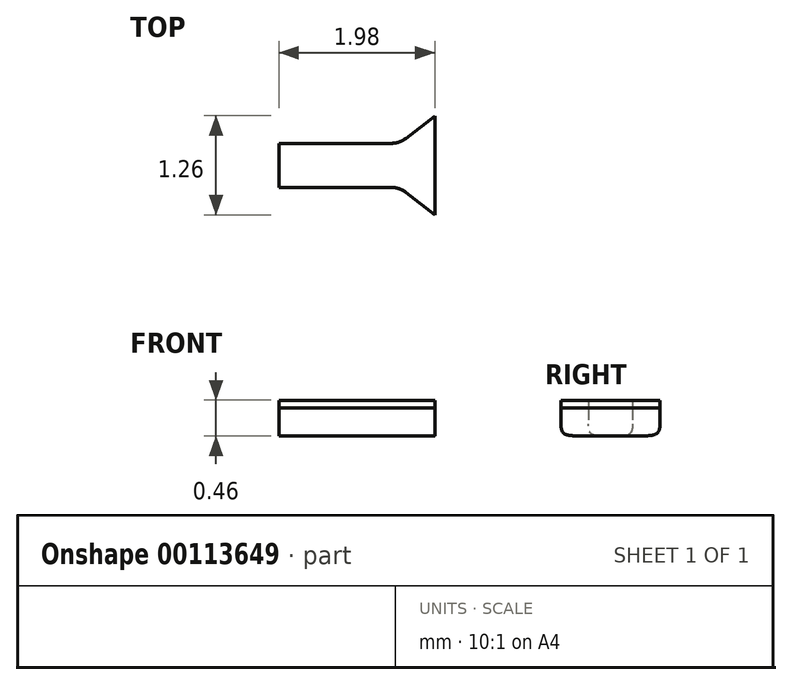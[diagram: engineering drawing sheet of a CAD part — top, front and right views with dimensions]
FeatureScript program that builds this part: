
annotation { "Feature Type Name" : "Feature", "Feature Type Description" : "" }
export const myFeature = defineFeature(function(context is Context, id is Id, definition is map)
    precondition{}
    {
        {
            var Q0;
            Q0=qCreatedBy(makeId("Top.planeOp"),FACE);
            var sketch = newSketch(context, id + "F0", { "sketchPlane" : qUnion([Q0])});
            skLineSegment(sketch, "E0", {"start": v(-7, 0) * mm, "end": v(-7, 1.25) * mm});
            skLineSegment(sketch, "E1", {"start": v(-7, 1.25) * mm, "end": v(-2.5, 1.25) * mm});
            skLineSegment(sketch, "E2", {"start": v(-2.5, 1.25) * mm, "end": v(-1.33, 0.34) * mm});
            skLineSegment(sketch, "E3", {"start": v(-1.15, 0.28) * mm, "end": v(0, 0.28) * mm});
            skPoint(sketch, "E4.visualSharp", {"position": v(-1.25, 0.28) * mm});
            skArc(sketch, "E4.filletArc", {"start": v(-1.33, 0.34) * mm, "mid": v(-1.24, 0.3) * mm, "end": v(-1.15, 0.28) * mm});
            skLineSegment(sketch, "E5.MirrorCS", {"start": v(-7, 0) * mm, "end": v(-7, -1.25) * mm});
            skLineSegment(sketch, "E6.MirrorCS", {"start": v(-7, -1.25) * mm, "end": v(-2.5, -1.25) * mm});
            skLineSegment(sketch, "E7.MirrorCS", {"start": v(-2.5, -1.25) * mm, "end": v(-1.33, -0.34) * mm});
            skLineSegment(sketch, "E8.MirrorCS", {"start": v(-1.15, -0.28) * mm, "end": v(0, -0.28) * mm});
            skArc(sketch, "E9.MirrorCS", {"start": v(-1.33, -0.34) * mm, "mid": v(-1.24, -0.3) * mm, "end": v(-1.15, -0.28) * mm});
            skCircle(sketch, "E10", {"center": v(-5, 0) * mm, "radius": 0.5 * mm});
            skArc(sketch, "E11.MirrorCS", {"start": v(1.33, -0.34) * mm, "mid": v(1.24, -0.3) * mm, "end": v(1.15, -0.28) * mm});
            skArc(sketch, "E12.MirrorCS", {"start": v(1.33, 0.34) * mm, "mid": v(1.24, 0.3) * mm, "end": v(1.15, 0.28) * mm});
            skLineSegment(sketch, "E13.MirrorCS", {"start": v(7, 0) * mm, "end": v(7, 1.25) * mm});
            skLineSegment(sketch, "E14.MirrorCS", {"start": v(7, 1.25) * mm, "end": v(2.5, 1.25) * mm});
            skLineSegment(sketch, "E15.MirrorCS", {"start": v(2.5, 1.25) * mm, "end": v(1.33, 0.34) * mm});
            skPoint(sketch, "E16.MirrorP", {"position": v(1.25, 0.28) * mm});
            skCircle(sketch, "E17.MirrorC", {"center": v(5, 0) * mm, "radius": 0.5 * mm});
            skLineSegment(sketch, "E18.MirrorCS", {"start": v(1.15, -0.28) * mm, "end": v(0, -0.28) * mm});
            skLineSegment(sketch, "E19.MirrorCS", {"start": v(2.5, -1.25) * mm, "end": v(1.33, -0.34) * mm});
            skLineSegment(sketch, "E20.MirrorCS", {"start": v(1.15, 0.28) * mm, "end": v(0, 0.28) * mm});
            skLineSegment(sketch, "E21.MirrorCS", {"start": v(7, 0) * mm, "end": v(7, -1.25) * mm});
            skLineSegment(sketch, "E22.MirrorCS", {"start": v(7, -1.25) * mm, "end": v(2.5, -1.25) * mm});
            skSolve(sketch);
        }
        {
            var Q0;
            Q0=makeQuery(id+"F0.imprint","IMPRINT",FACE,{"disambiguationData":[TD([[makeQuery(id+"F0.imprint","IMPRINT",EDGE,{"derivedFrom":sQuery(id+"F0.wireOp",EDGE,"E0")}),-1.0]])]});
            extrude(context, id + "F1", {"entities" : qUnion([Q0]), "depth" : 0.35 * mm, "offsetDistance" : 25 * mm, "symmetric" : true});
        }
        {
            var Q0;
            Q0=makeQuery(id+"F1.opExtrude","SWEPT_EDGE",EDGE,{"disambiguationData":[OSD([sQuery(id+"F0.wireOp",EDGE,"E6.MirrorCS"),sQuery(id+"F0.wireOp",EDGE,"E7.MirrorCS")])]});
            var Q1;
            Q1=makeQuery(id+"F1.opExtrude","SWEPT_EDGE",EDGE,{"disambiguationData":[OSD([sQuery(id+"F0.wireOp",EDGE,"E19.MirrorCS"),sQuery(id+"F0.wireOp",EDGE,"E22.MirrorCS")])]});
            var Q2;
            Q2=makeQuery(id+"F1.opExtrude","SWEPT_EDGE",EDGE,{"disambiguationData":[OSD([sQuery(id+"F0.wireOp",EDGE,"E1"),sQuery(id+"F0.wireOp",EDGE,"E2")])]});
            var Q3;
            Q3=makeQuery(id+"F1.opExtrude","SWEPT_EDGE",EDGE,{"disambiguationData":[OSD([sQuery(id+"F0.wireOp",EDGE,"E14.MirrorCS"),sQuery(id+"F0.wireOp",EDGE,"E15.MirrorCS")])]});
            fillet(context, id + "F2", {"entities" : qUnion([Q0, Q1, Q2, Q3]), "radius" : 0.3 * mm, "tangentPropagation" : true, "allowEdgeOverflow" : false});
        }
        {
            var Q0;
            Q0=qCreatedBy(makeId("Top.planeOp"),FACE);
            var sketch = newSketch(context, id + "F3", { "sketchPlane" : qUnion([Q0])});
            skLineSegment(sketch, "E23.bottom", {"start": v(-0.28, -1.5) * mm, "end": v(1.7, -1.5) * mm});
            skLineSegment(sketch, "E23.top", {"start": v(-0.28, 1.5) * mm, "end": v(1.7, 1.5) * mm});
            skLineSegment(sketch, "E23.left", {"start": v(-0.28, -1.5) * mm, "end": v(-0.28, 1.5) * mm});
            skLineSegment(sketch, "E23.right", {"start": v(1.7, -1.5) * mm, "end": v(1.7, 1.5) * mm});
            skSolve(sketch);
        }
        {
            var Q0;
            Q0=makeQuery(id+"F3.imprint","IMPRINT",FACE,{"disambiguationData":[TD([[makeQuery(id+"F3.imprint","IMPRINT",EDGE,{"derivedFrom":sQuery(id+"F3.wireOp",EDGE,"E23.bottom")}),1.0]])]});
            extrude(context, id + "F4", {"entities" : qUnion([Q0]), "depth" : 1 * mm, "offsetDistance" : 25 * mm, "symmetric" : true});
        }
        {
            var Q0;
            Q0=makeQuery(id+"F4.opExtrude","SWEPT_BODY",BODY,{"disambiguationData":[OSD([sQuery(id+"F3.wireOp",EDGE,"E23.bottom"),sQuery(id+"F3.wireOp",EDGE,"E23.top"),sQuery(id+"F3.wireOp",EDGE,"E23.right"),sQuery(id+"F3.wireOp",EDGE,"E23.left")])]});
            var Q1;
            Q1=makeQuery(id+"F1.opExtrude","SWEPT_BODY",BODY,{"disambiguationData":[OSD([sQuery(id+"F0.wireOp",EDGE,"E0"),sQuery(id+"F0.wireOp",EDGE,"E1"),sQuery(id+"F0.wireOp",EDGE,"E2"),sQuery(id+"F0.wireOp",EDGE,"E3"),sQuery(id+"F0.wireOp",EDGE,"E4.filletArc"),sQuery(id+"F0.wireOp",EDGE,"E5.MirrorCS"),sQuery(id+"F0.wireOp",EDGE,"E6.MirrorCS"),sQuery(id+"F0.wireOp",EDGE,"E7.MirrorCS"),sQuery(id+"F0.wireOp",EDGE,"E8.MirrorCS"),sQuery(id+"F0.wireOp",EDGE,"E9.MirrorCS"),sQuery(id+"F0.wireOp",EDGE,"E10"),sQuery(id+"F0.wireOp",EDGE,"E11.MirrorCS"),sQuery(id+"F0.wireOp",EDGE,"E12.MirrorCS"),sQuery(id+"F0.wireOp",EDGE,"E13.MirrorCS"),sQuery(id+"F0.wireOp",EDGE,"E14.MirrorCS"),sQuery(id+"F0.wireOp",EDGE,"E15.MirrorCS"),sQuery(id+"F0.wireOp",EDGE,"E17.MirrorC"),sQuery(id+"F0.wireOp",EDGE,"E18.MirrorCS"),sQuery(id+"F0.wireOp",EDGE,"E19.MirrorCS"),sQuery(id+"F0.wireOp",EDGE,"E20.MirrorCS"),sQuery(id+"F0.wireOp",EDGE,"E21.MirrorCS"),sQuery(id+"F0.wireOp",EDGE,"E22.MirrorCS")])]});
            booleanBodies(context, id + "F5", {"operationType" : BooleanOperationType.INTERSECTION, "tools" : qUnion([Q0, Q1])});
        }
        {
            var Q0;
            Q0=makeQuery(id+"F1.opExtrude","CAP_FACE",FACE,{"disambiguationData":[OSD([sQuery(id+"F0.wireOp",EDGE,"E0"),sQuery(id+"F0.wireOp",EDGE,"E1"),sQuery(id+"F0.wireOp",EDGE,"E2"),sQuery(id+"F0.wireOp",EDGE,"E3"),sQuery(id+"F0.wireOp",EDGE,"E4.filletArc"),sQuery(id+"F0.wireOp",EDGE,"E5.MirrorCS"),sQuery(id+"F0.wireOp",EDGE,"E6.MirrorCS"),sQuery(id+"F0.wireOp",EDGE,"E7.MirrorCS"),sQuery(id+"F0.wireOp",EDGE,"E8.MirrorCS"),sQuery(id+"F0.wireOp",EDGE,"E9.MirrorCS"),sQuery(id+"F0.wireOp",EDGE,"E10"),sQuery(id+"F0.wireOp",EDGE,"E11.MirrorCS"),sQuery(id+"F0.wireOp",EDGE,"E12.MirrorCS"),sQuery(id+"F0.wireOp",EDGE,"E13.MirrorCS"),sQuery(id+"F0.wireOp",EDGE,"E14.MirrorCS"),sQuery(id+"F0.wireOp",EDGE,"E15.MirrorCS"),sQuery(id+"F0.wireOp",EDGE,"E17.MirrorC"),sQuery(id+"F0.wireOp",EDGE,"E18.MirrorCS"),sQuery(id+"F0.wireOp",EDGE,"E19.MirrorCS"),sQuery(id+"F0.wireOp",EDGE,"E20.MirrorCS"),sQuery(id+"F0.wireOp",EDGE,"E21.MirrorCS"),sQuery(id+"F0.wireOp",EDGE,"E22.MirrorCS")])],"isStart":false});
            extrude(context, id + "F6", {"entities" : qUnion([Q0]), "depth" : 0.1 * mm, "offsetDistance" : 25 * mm});
        }
        {
            var Q0;
            Q0=makeQuery(id+"F5.opBoolean","COPY",EDGE,{"derivedFrom":makeQuery(id+"F1.opExtrude","CAP_EDGE",EDGE,{"disambiguationData":[OSD([sQuery(id+"F0.wireOp",EDGE,"E8.MirrorCS"),sQuery(id+"F0.wireOp",EDGE,"E18.MirrorCS")])],"isStart":false})});
            var Q1;
            Q1=makeQuery(id+"F5.opBoolean","COPY",EDGE,{"derivedFrom":makeQuery(id+"F1.opExtrude","CAP_EDGE",EDGE,{"disambiguationData":[OSD([sQuery(id+"F0.wireOp",EDGE,"E3"),sQuery(id+"F0.wireOp",EDGE,"E20.MirrorCS")])],"isStart":false})});
            var Q2;
            Q2=makeQuery(id+"F1.opExtrude","CAP_EDGE",EDGE,{"disambiguationData":[OSD([sQuery(id+"F0.wireOp",EDGE,"E3"),sQuery(id+"F0.wireOp",EDGE,"E20.MirrorCS")])],"isStart":true});
            var Q3;
            Q3=makeQuery(id+"F1.opExtrude","CAP_EDGE",EDGE,{"disambiguationData":[OSD([sQuery(id+"F0.wireOp",EDGE,"E8.MirrorCS"),sQuery(id+"F0.wireOp",EDGE,"E18.MirrorCS")])],"isStart":true});
            fillet(context, id + "F7", {"entities" : qUnion([Q0, Q1, Q2, Q3]), "radius" : 0.15 * mm, "tangentPropagation" : true, "rho" : 0.6, "crossSection" : FilletCrossSection.CONIC, "allowEdgeOverflow" : false});
        }
    });
